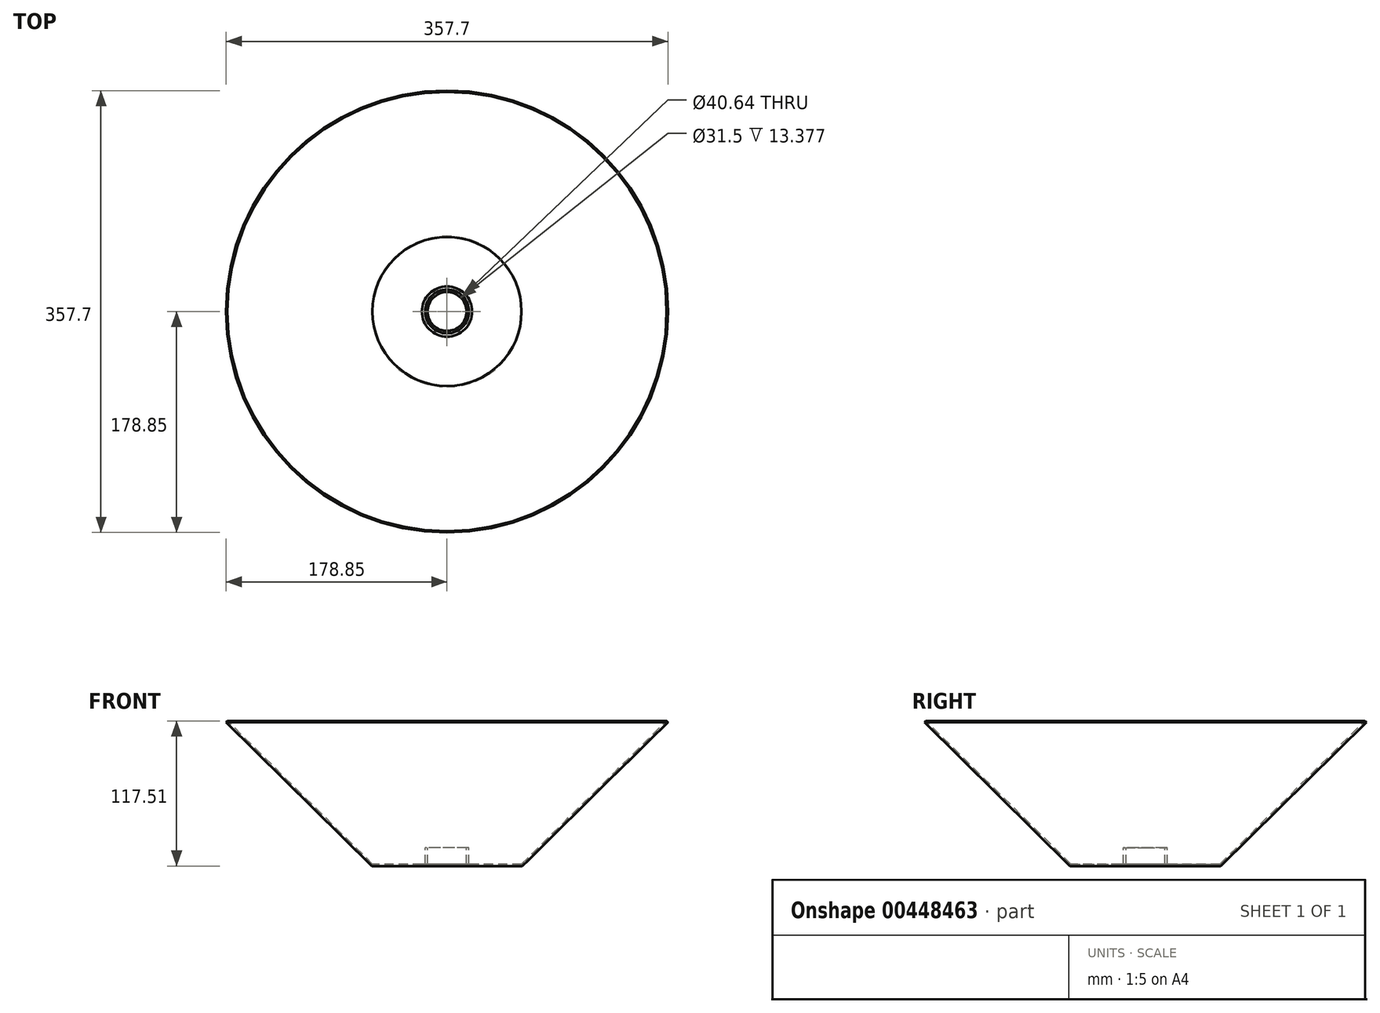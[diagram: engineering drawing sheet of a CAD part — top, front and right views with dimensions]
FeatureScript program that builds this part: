
annotation { "Feature Type Name" : "Feature", "Feature Type Description" : "" }
export const myFeature = defineFeature(function(context is Context, id is Id, definition is map)
    precondition{}
    {
        {
            var Q0;
            Q0=qCreatedBy(makeId("Front.planeOp"),FACE);
            var sketch = newSketch(context, id + "F0", { "sketchPlane" : qUnion([Q0])});
            skPoint(sketch, "E0", {"position": v(-60.33, 0) * mm});
            skPoint(sketch, "E1", {"position": v(-20.32, 0) * mm});
            skLineSegment(sketch, "E2", {"start": v(-60.33, 0) * mm, "end": v(-20.32, 0) * mm});
            skPoint(sketch, "E3", {"position": v(-177.8, 116) * mm});
            skPoint(sketch, "E4", {"position": v(0, 116) * mm});
            skLineSegment(sketch, "E5", {"start": v(-177.8, 116) * mm, "end": v(-60.32, 0) * mm});
            skLineSegment(sketch, "E6.0", {"start": v(-60.94, -1.5) * mm, "end": v(-20.32, -1.5) * mm});
            skLineSegment(sketch, "E6.1", {"start": v(-178.85, 114.94) * mm, "end": v(-60.94, -1.5) * mm});
            skLineSegment(sketch, "E7", {"start": v(-178.85, 114.94) * mm, "end": v(-177.8, 116) * mm});
            skLineSegment(sketch, "E8", {"start": v(-20.32, 0) * mm, "end": v(-20.32, -1.5) * mm});
            skLineSegment(sketch, "E9", {"start": v(0, 116) * mm, "end": v(0, 0) * mm, "construction": true});
            skPoint(sketch, "E10", {"position": v(-17.75, 0) * mm});
            skLineSegment(sketch, "E11", {"start": v(-17.75, 0) * mm, "end": v(-17.75, 13.38) * mm});
            skLineSegment(sketch, "E12.0", {"start": v(-15.75, 0) * mm, "end": v(-15.75, 13.38) * mm});
            skLineSegment(sketch, "E13", {"start": v(-17.75, 13.38) * mm, "end": v(-15.75, 13.38) * mm});
            skLineSegment(sketch, "E14", {"start": v(-17.75, 0) * mm, "end": v(-15.75, 0) * mm});
            skSolve(sketch);
        }
        {
            var Q0;
            Q0 = qSketchRegion(id + "F0", true);
            var Q1;
            Q1=sQuery(id+"F0.wireOp",EDGE,"E9");
            revolve(context, id + "F1", {"entities" : qUnion([Q0]), "axis" : qUnion([Q1]), "revolveType" : RevolveType.FULL});
        }
    });
